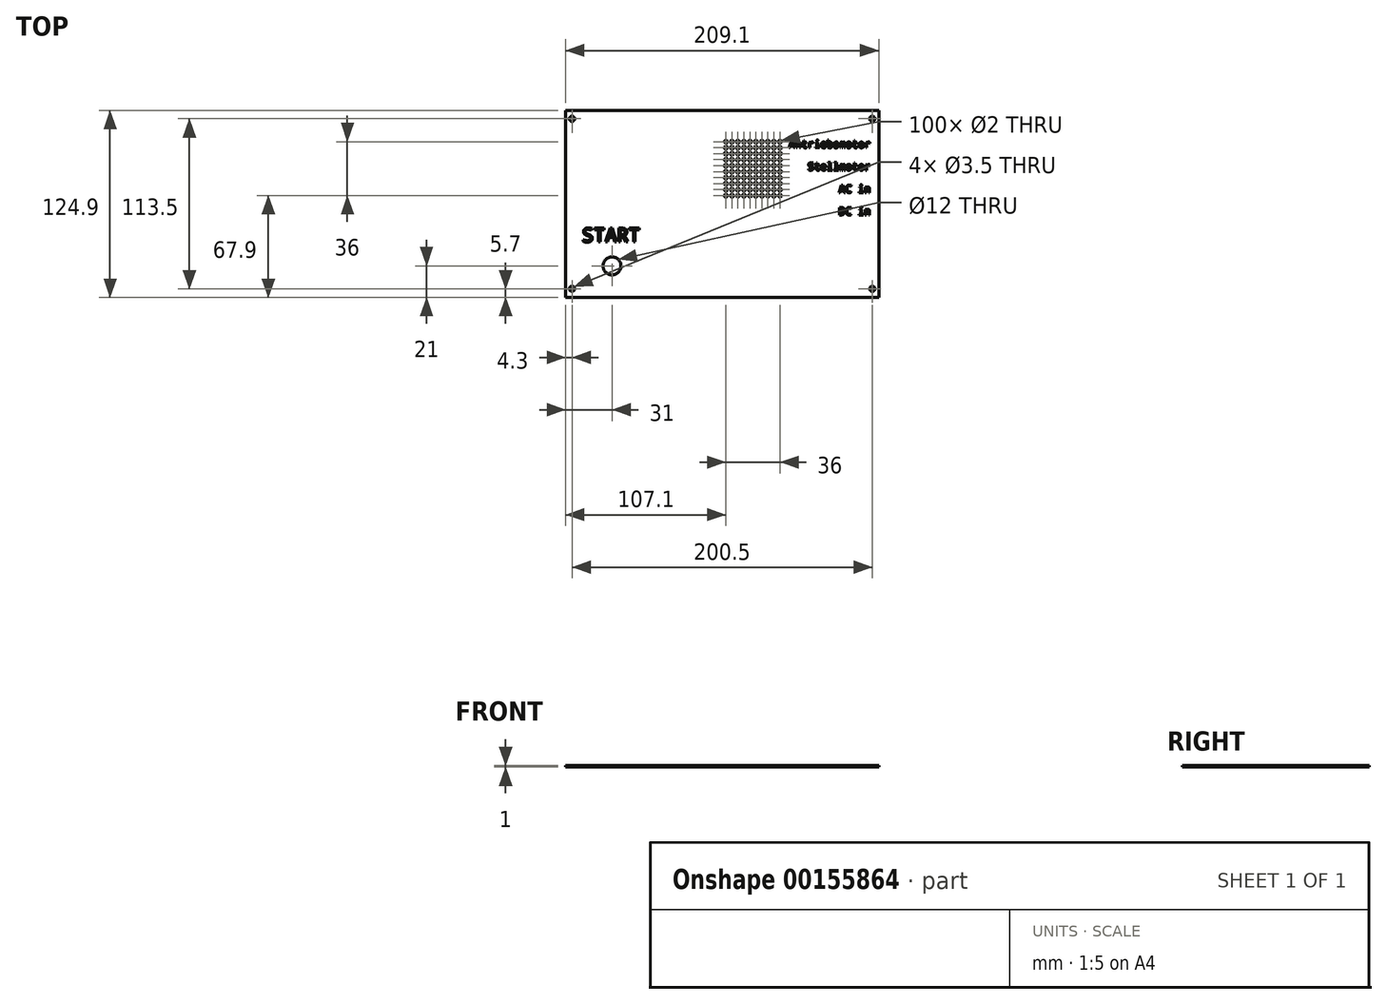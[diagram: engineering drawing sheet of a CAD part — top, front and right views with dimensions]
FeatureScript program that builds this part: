
annotation { "Feature Type Name" : "Feature", "Feature Type Description" : "" }
export const myFeature = defineFeature(function(context is Context, id is Id, definition is map)
    precondition{}
    {
        {
            var Q0;
            Q0=qCreatedBy(makeId("Top.planeOp"),FACE);
            var sketch = newSketch(context, id + "F0", { "sketchPlane" : qUnion([Q0])});
            skLineSegment(sketch, "E0.bottom", {"start": v(104.55, 62.45) * mm, "end": v(-104.55, 62.45) * mm});
            skLineSegment(sketch, "E0.top", {"start": v(104.55, -62.45) * mm, "end": v(-104.55, -62.45) * mm});
            skLineSegment(sketch, "E0.left", {"start": v(104.55, 62.45) * mm, "end": v(104.55, -62.45) * mm});
            skLineSegment(sketch, "E0.right", {"start": v(-104.55, 62.45) * mm, "end": v(-104.55, -62.45) * mm});
            skSolve(sketch);
        }
        {
            var Q0;
            Q0 = qSketchRegion(id + "F0", true);
            extrude(context, id + "F1", {"entities" : qUnion([Q0]), "endBound" : BoundingType.SYMMETRIC, "depth" : 1 * mm});
        }
        {
            var Q0;
            Q0=makeQuery(id+"F1.opExtrude","CAP_FACE",FACE,{"disambiguationData":[OSD([sQuery(id+"F0.wireOp",EDGE,"E0.bottom"),sQuery(id+"F0.wireOp",EDGE,"E0.top"),sQuery(id+"F0.wireOp",EDGE,"E0.left"),sQuery(id+"F0.wireOp",EDGE,"E0.right")])],"isStart":false});
            var sketch = newSketch(context, id + "F2", { "sketchPlane" : qUnion([Q0])});
            skLineSegment(sketch, "E1.bottom", {"start": v(100.25, 56.75) * mm, "end": v(-100.25, 56.75) * mm, "construction": true});
            skLineSegment(sketch, "E1.top", {"start": v(100.25, -56.75) * mm, "end": v(-100.25, -56.75) * mm, "construction": true});
            skLineSegment(sketch, "E1.left", {"start": v(100.25, 56.75) * mm, "end": v(100.25, -56.75) * mm, "construction": true});
            skLineSegment(sketch, "E1.right", {"start": v(-100.25, 56.75) * mm, "end": v(-100.25, -56.75) * mm, "construction": true});
            skPoint(sketch, "E1.middle", {"position": v(0, 0) * mm});
            skCircle(sketch, "E2", {"center": v(-100.25, 56.75) * mm, "radius": 1.75 * mm});
            skCircle(sketch, "E3", {"center": v(100.25, 56.75) * mm, "radius": 1.75 * mm});
            skCircle(sketch, "E4", {"center": v(100.25, -56.75) * mm, "radius": 1.75 * mm});
            skCircle(sketch, "E5", {"center": v(-100.25, -56.75) * mm, "radius": 1.75 * mm});
            skSolve(sketch);
        }
        {
            var Q0;
            Q0 = qSketchRegion(id + "F2", true);
            extrude(context, id + "F3", {"entities" : qUnion([Q0]), "operationType" : NewBodyOperationType.REMOVE, "endBound" : BoundingType.THROUGH_ALL, "oppositeDirection" : true, "depth" : 25 * mm});
        }
        {
            var Q0;
            Q0=makeQuery(id+"F1.opExtrude","CAP_FACE",FACE,{"disambiguationData":[OSD([sQuery(id+"F0.wireOp",EDGE,"E0.bottom"),sQuery(id+"F0.wireOp",EDGE,"E0.top"),sQuery(id+"F0.wireOp",EDGE,"E0.left"),sQuery(id+"F0.wireOp",EDGE,"E0.right")])],"isStart":false});
            var sketch = newSketch(context, id + "F4", { "sketchPlane" : qUnion([Q0])});
            skCircle(sketch, "E6", {"center": v(2.55, 41.45) * mm, "radius": 1 * mm});
            skCircle(sketch, "E7.0.1.0", {"center": v(2.55, 37.45) * mm, "radius": 1 * mm});
            skCircle(sketch, "E7.0.2.0", {"center": v(2.55, 33.45) * mm, "radius": 1 * mm});
            skCircle(sketch, "E7.0.3.0", {"center": v(2.55, 29.45) * mm, "radius": 1 * mm});
            skCircle(sketch, "E7.0.4.0", {"center": v(2.55, 25.45) * mm, "radius": 1 * mm});
            skCircle(sketch, "E7.0.5.0", {"center": v(2.55, 21.45) * mm, "radius": 1 * mm});
            skCircle(sketch, "E7.0.6.0", {"center": v(2.55, 17.45) * mm, "radius": 1 * mm});
            skCircle(sketch, "E7.0.7.0", {"center": v(2.55, 13.45) * mm, "radius": 1 * mm});
            skCircle(sketch, "E7.0.8.0", {"center": v(2.55, 9.45) * mm, "radius": 1 * mm});
            skCircle(sketch, "E7.0.9.0", {"center": v(2.55, 5.45) * mm, "radius": 1 * mm});
            skCircle(sketch, "E7.1.0.0", {"center": v(6.55, 41.45) * mm, "radius": 1 * mm});
            skCircle(sketch, "E7.1.1.0", {"center": v(6.55, 37.45) * mm, "radius": 1 * mm});
            skCircle(sketch, "E7.1.2.0", {"center": v(6.55, 33.45) * mm, "radius": 1 * mm});
            skCircle(sketch, "E7.1.3.0", {"center": v(6.55, 29.45) * mm, "radius": 1 * mm});
            skCircle(sketch, "E7.1.4.0", {"center": v(6.55, 25.45) * mm, "radius": 1 * mm});
            skCircle(sketch, "E7.1.5.0", {"center": v(6.55, 21.45) * mm, "radius": 1 * mm});
            skCircle(sketch, "E7.1.6.0", {"center": v(6.55, 17.45) * mm, "radius": 1 * mm});
            skCircle(sketch, "E7.1.7.0", {"center": v(6.55, 13.45) * mm, "radius": 1 * mm});
            skCircle(sketch, "E7.1.8.0", {"center": v(6.55, 9.45) * mm, "radius": 1 * mm});
            skCircle(sketch, "E7.1.9.0", {"center": v(6.55, 5.45) * mm, "radius": 1 * mm});
            skCircle(sketch, "E7.2.0.0", {"center": v(10.55, 41.45) * mm, "radius": 1 * mm});
            skCircle(sketch, "E7.2.1.0", {"center": v(10.55, 37.45) * mm, "radius": 1 * mm});
            skCircle(sketch, "E7.2.2.0", {"center": v(10.55, 33.45) * mm, "radius": 1 * mm});
            skCircle(sketch, "E7.2.3.0", {"center": v(10.55, 29.45) * mm, "radius": 1 * mm});
            skCircle(sketch, "E7.2.4.0", {"center": v(10.55, 25.45) * mm, "radius": 1 * mm});
            skCircle(sketch, "E7.2.5.0", {"center": v(10.55, 21.45) * mm, "radius": 1 * mm});
            skCircle(sketch, "E7.2.6.0", {"center": v(10.55, 17.45) * mm, "radius": 1 * mm});
            skCircle(sketch, "E7.2.7.0", {"center": v(10.55, 13.45) * mm, "radius": 1 * mm});
            skCircle(sketch, "E7.2.8.0", {"center": v(10.55, 9.45) * mm, "radius": 1 * mm});
            skCircle(sketch, "E7.2.9.0", {"center": v(10.55, 5.45) * mm, "radius": 1 * mm});
            skCircle(sketch, "E7.3.0.0", {"center": v(14.55, 41.45) * mm, "radius": 1 * mm});
            skCircle(sketch, "E7.3.1.0", {"center": v(14.55, 37.45) * mm, "radius": 1 * mm});
            skCircle(sketch, "E7.3.2.0", {"center": v(14.55, 33.45) * mm, "radius": 1 * mm});
            skCircle(sketch, "E7.3.3.0", {"center": v(14.55, 29.45) * mm, "radius": 1 * mm});
            skCircle(sketch, "E7.3.4.0", {"center": v(14.55, 25.45) * mm, "radius": 1 * mm});
            skCircle(sketch, "E7.3.5.0", {"center": v(14.55, 21.45) * mm, "radius": 1 * mm});
            skCircle(sketch, "E7.3.6.0", {"center": v(14.55, 17.45) * mm, "radius": 1 * mm});
            skCircle(sketch, "E7.3.7.0", {"center": v(14.55, 13.45) * mm, "radius": 1 * mm});
            skCircle(sketch, "E7.3.8.0", {"center": v(14.55, 9.45) * mm, "radius": 1 * mm});
            skCircle(sketch, "E7.3.9.0", {"center": v(14.55, 5.45) * mm, "radius": 1 * mm});
            skCircle(sketch, "E7.4.0.0", {"center": v(18.55, 41.45) * mm, "radius": 1 * mm});
            skCircle(sketch, "E7.4.1.0", {"center": v(18.55, 37.45) * mm, "radius": 1 * mm});
            skCircle(sketch, "E7.4.2.0", {"center": v(18.55, 33.45) * mm, "radius": 1 * mm});
            skCircle(sketch, "E7.4.3.0", {"center": v(18.55, 29.45) * mm, "radius": 1 * mm});
            skCircle(sketch, "E7.4.4.0", {"center": v(18.55, 25.45) * mm, "radius": 1 * mm});
            skCircle(sketch, "E7.4.5.0", {"center": v(18.55, 21.45) * mm, "radius": 1 * mm});
            skCircle(sketch, "E7.4.6.0", {"center": v(18.55, 17.45) * mm, "radius": 1 * mm});
            skCircle(sketch, "E7.4.7.0", {"center": v(18.55, 13.45) * mm, "radius": 1 * mm});
            skCircle(sketch, "E7.4.8.0", {"center": v(18.55, 9.45) * mm, "radius": 1 * mm});
            skCircle(sketch, "E7.4.9.0", {"center": v(18.55, 5.45) * mm, "radius": 1 * mm});
            skCircle(sketch, "E7.5.0.0", {"center": v(22.55, 41.45) * mm, "radius": 1 * mm});
            skCircle(sketch, "E7.5.1.0", {"center": v(22.55, 37.45) * mm, "radius": 1 * mm});
            skCircle(sketch, "E7.5.2.0", {"center": v(22.55, 33.45) * mm, "radius": 1 * mm});
            skCircle(sketch, "E7.5.3.0", {"center": v(22.55, 29.45) * mm, "radius": 1 * mm});
            skCircle(sketch, "E7.5.4.0", {"center": v(22.55, 25.45) * mm, "radius": 1 * mm});
            skCircle(sketch, "E7.5.5.0", {"center": v(22.55, 21.45) * mm, "radius": 1 * mm});
            skCircle(sketch, "E7.5.6.0", {"center": v(22.55, 17.45) * mm, "radius": 1 * mm});
            skCircle(sketch, "E7.5.7.0", {"center": v(22.55, 13.45) * mm, "radius": 1 * mm});
            skCircle(sketch, "E7.5.8.0", {"center": v(22.55, 9.45) * mm, "radius": 1 * mm});
            skCircle(sketch, "E7.5.9.0", {"center": v(22.55, 5.45) * mm, "radius": 1 * mm});
            skCircle(sketch, "E7.6.0.0", {"center": v(26.55, 41.45) * mm, "radius": 1 * mm});
            skCircle(sketch, "E7.6.1.0", {"center": v(26.55, 37.45) * mm, "radius": 1 * mm});
            skCircle(sketch, "E7.6.2.0", {"center": v(26.55, 33.45) * mm, "radius": 1 * mm});
            skCircle(sketch, "E7.6.3.0", {"center": v(26.55, 29.45) * mm, "radius": 1 * mm});
            skCircle(sketch, "E7.6.4.0", {"center": v(26.55, 25.45) * mm, "radius": 1 * mm});
            skCircle(sketch, "E7.6.5.0", {"center": v(26.55, 21.45) * mm, "radius": 1 * mm});
            skCircle(sketch, "E7.6.6.0", {"center": v(26.55, 17.45) * mm, "radius": 1 * mm});
            skCircle(sketch, "E7.6.7.0", {"center": v(26.55, 13.45) * mm, "radius": 1 * mm});
            skCircle(sketch, "E7.6.8.0", {"center": v(26.55, 9.45) * mm, "radius": 1 * mm});
            skCircle(sketch, "E7.6.9.0", {"center": v(26.55, 5.45) * mm, "radius": 1 * mm});
            skCircle(sketch, "E7.7.0.0", {"center": v(30.55, 41.45) * mm, "radius": 1 * mm});
            skCircle(sketch, "E7.7.1.0", {"center": v(30.55, 37.45) * mm, "radius": 1 * mm});
            skCircle(sketch, "E7.7.2.0", {"center": v(30.55, 33.45) * mm, "radius": 1 * mm});
            skCircle(sketch, "E7.7.3.0", {"center": v(30.55, 29.45) * mm, "radius": 1 * mm});
            skCircle(sketch, "E7.7.4.0", {"center": v(30.55, 25.45) * mm, "radius": 1 * mm});
            skCircle(sketch, "E7.7.5.0", {"center": v(30.55, 21.45) * mm, "radius": 1 * mm});
            skCircle(sketch, "E7.7.6.0", {"center": v(30.55, 17.45) * mm, "radius": 1 * mm});
            skCircle(sketch, "E7.7.7.0", {"center": v(30.55, 13.45) * mm, "radius": 1 * mm});
            skCircle(sketch, "E7.7.8.0", {"center": v(30.55, 9.45) * mm, "radius": 1 * mm});
            skCircle(sketch, "E7.7.9.0", {"center": v(30.55, 5.45) * mm, "radius": 1 * mm});
            skCircle(sketch, "E7.8.0.0", {"center": v(34.55, 41.45) * mm, "radius": 1 * mm});
            skCircle(sketch, "E7.8.1.0", {"center": v(34.55, 37.45) * mm, "radius": 1 * mm});
            skCircle(sketch, "E7.8.2.0", {"center": v(34.55, 33.45) * mm, "radius": 1 * mm});
            skCircle(sketch, "E7.8.3.0", {"center": v(34.55, 29.45) * mm, "radius": 1 * mm});
            skCircle(sketch, "E7.8.4.0", {"center": v(34.55, 25.45) * mm, "radius": 1 * mm});
            skCircle(sketch, "E7.8.5.0", {"center": v(34.55, 21.45) * mm, "radius": 1 * mm});
            skCircle(sketch, "E7.8.6.0", {"center": v(34.55, 17.45) * mm, "radius": 1 * mm});
            skCircle(sketch, "E7.8.7.0", {"center": v(34.55, 13.45) * mm, "radius": 1 * mm});
            skCircle(sketch, "E7.8.8.0", {"center": v(34.55, 9.45) * mm, "radius": 1 * mm});
            skCircle(sketch, "E7.8.9.0", {"center": v(34.55, 5.45) * mm, "radius": 1 * mm});
            skCircle(sketch, "E7.9.0.0", {"center": v(38.55, 41.45) * mm, "radius": 1 * mm});
            skCircle(sketch, "E7.9.1.0", {"center": v(38.55, 37.45) * mm, "radius": 1 * mm});
            skCircle(sketch, "E7.9.2.0", {"center": v(38.55, 33.45) * mm, "radius": 1 * mm});
            skCircle(sketch, "E7.9.3.0", {"center": v(38.55, 29.45) * mm, "radius": 1 * mm});
            skCircle(sketch, "E7.9.4.0", {"center": v(38.55, 25.45) * mm, "radius": 1 * mm});
            skCircle(sketch, "E7.9.5.0", {"center": v(38.55, 21.45) * mm, "radius": 1 * mm});
            skCircle(sketch, "E7.9.6.0", {"center": v(38.55, 17.45) * mm, "radius": 1 * mm});
            skCircle(sketch, "E7.9.7.0", {"center": v(38.55, 13.45) * mm, "radius": 1 * mm});
            skCircle(sketch, "E7.9.8.0", {"center": v(38.55, 9.45) * mm, "radius": 1 * mm});
            skCircle(sketch, "E7.9.9.0", {"center": v(38.55, 5.45) * mm, "radius": 1 * mm});
            skLineSegment(sketch, "E7.direction1", {"start": v(2.55, 41.45) * mm, "end": v(6.55, 41.45) * mm, "construction": true});
            skLineSegment(sketch, "E7.direction2", {"start": v(2.55, 41.45) * mm, "end": v(2.55, 37.45) * mm, "construction": true});
            skSolve(sketch);
        }
        {
            var Q0;
            Q0 = qSketchRegion(id + "F4", true);
            extrude(context, id + "F5", {"entities" : qUnion([Q0]), "operationType" : NewBodyOperationType.REMOVE, "endBound" : BoundingType.THROUGH_ALL, "oppositeDirection" : true, "depth" : 25 * mm});
        }
        {
            var Q0;
            Q0=makeQuery(id+"F1.opExtrude","CAP_FACE",FACE,{"disambiguationData":[OSD([sQuery(id+"F0.wireOp",EDGE,"E0.bottom"),sQuery(id+"F0.wireOp",EDGE,"E0.top"),sQuery(id+"F0.wireOp",EDGE,"E0.left"),sQuery(id+"F0.wireOp",EDGE,"E0.right")])],"isStart":false});
            var sketch = newSketch(context, id + "F6", { "sketchPlane" : qUnion([Q0])});
            skCircle(sketch, "E8", {"center": v(-73.55, -41.45) * mm, "radius": 6 * mm});
            skSolve(sketch);
        }
        {
            var Q0;
            Q0 = qSketchRegion(id + "F6", true);
            extrude(context, id + "F7", {"entities" : qUnion([Q0]), "operationType" : NewBodyOperationType.REMOVE, "endBound" : BoundingType.THROUGH_ALL, "oppositeDirection" : true, "depth" : 25 * mm});
        }
        {
            var Q0;
            Q0=makeQuery(id+"F1.opExtrude","CAP_FACE",FACE,{"disambiguationData":[OSD([sQuery(id+"F0.wireOp",EDGE,"E0.bottom"),sQuery(id+"F0.wireOp",EDGE,"E0.top"),sQuery(id+"F0.wireOp",EDGE,"E0.left"),sQuery(id+"F0.wireOp",EDGE,"E0.right")])],"isStart":false});
            var sketch = newSketch(context, id + "F8", { "sketchPlane" : qUnion([Q0])});
            skText(sketch, "E9", { "text": "Antriebsmotor", "fontName": "DroidSansMono.ttf"});
            skText(sketch, "E10", { "text": "Stellmotor", "fontName": "DroidSansMono.ttf"});
            skText(sketch, "E11", { "text": "AC in", "fontName": "DroidSansMono.ttf"});
            skText(sketch, "E12", { "text": "DC in", "fontName": "DroidSansMono.ttf"});
            skLineSegment(sketch, "E13", {"start": v(99.55, 37.4) * mm, "end": v(99.55, 27.5) * mm, "construction": true});
            skLineSegment(sketch, "E14", {"start": v(99.55, 22.45) * mm, "end": v(99.55, 12.55) * mm, "construction": true});
            skLineSegment(sketch, "E15", {"start": v(99.55, 7.5) * mm, "end": v(99.55, -2.4) * mm, "construction": true});
            skLineSegment(sketch, "E16", {"start": v(39.55, 41.45) * mm, "end": v(44.55, 41.45) * mm, "construction": true});
            skLineSegment(sketch, "E17", {"start": v(99.55, 39.93) * mm, "end": v(104.55, 39.93) * mm, "construction": true});
            skText(sketch, "E18", { "text": "START", "fontName": "DroidSansMono.ttf"});
            const initialGuessF8  = {"E9": [0.04455, 0.0374, 1, 0, 0.00505], "E10": [0.05717, 0.02245, 1, 0, 0.00505], "E11": [0.078, 0.0075, 1, 0, 0.00505], "E12": [0.078, -0.00745, 1, 0, 0.00505], "E18": [-0.09355, -0.02545, 1, 0, 0.0093]};
            skSetInitialGuess(sketch, initialGuessF8);
            skSolve(sketch);
        }
        {
            var Q0;
            Q0 = qSketchRegion(id + "F8", true);
            extrude(context, id + "F9", {"entities" : qUnion([Q0]), "operationType" : NewBodyOperationType.REMOVE, "oppositeDirection" : true, "depth" : 0.5 * mm});
        }
    });
